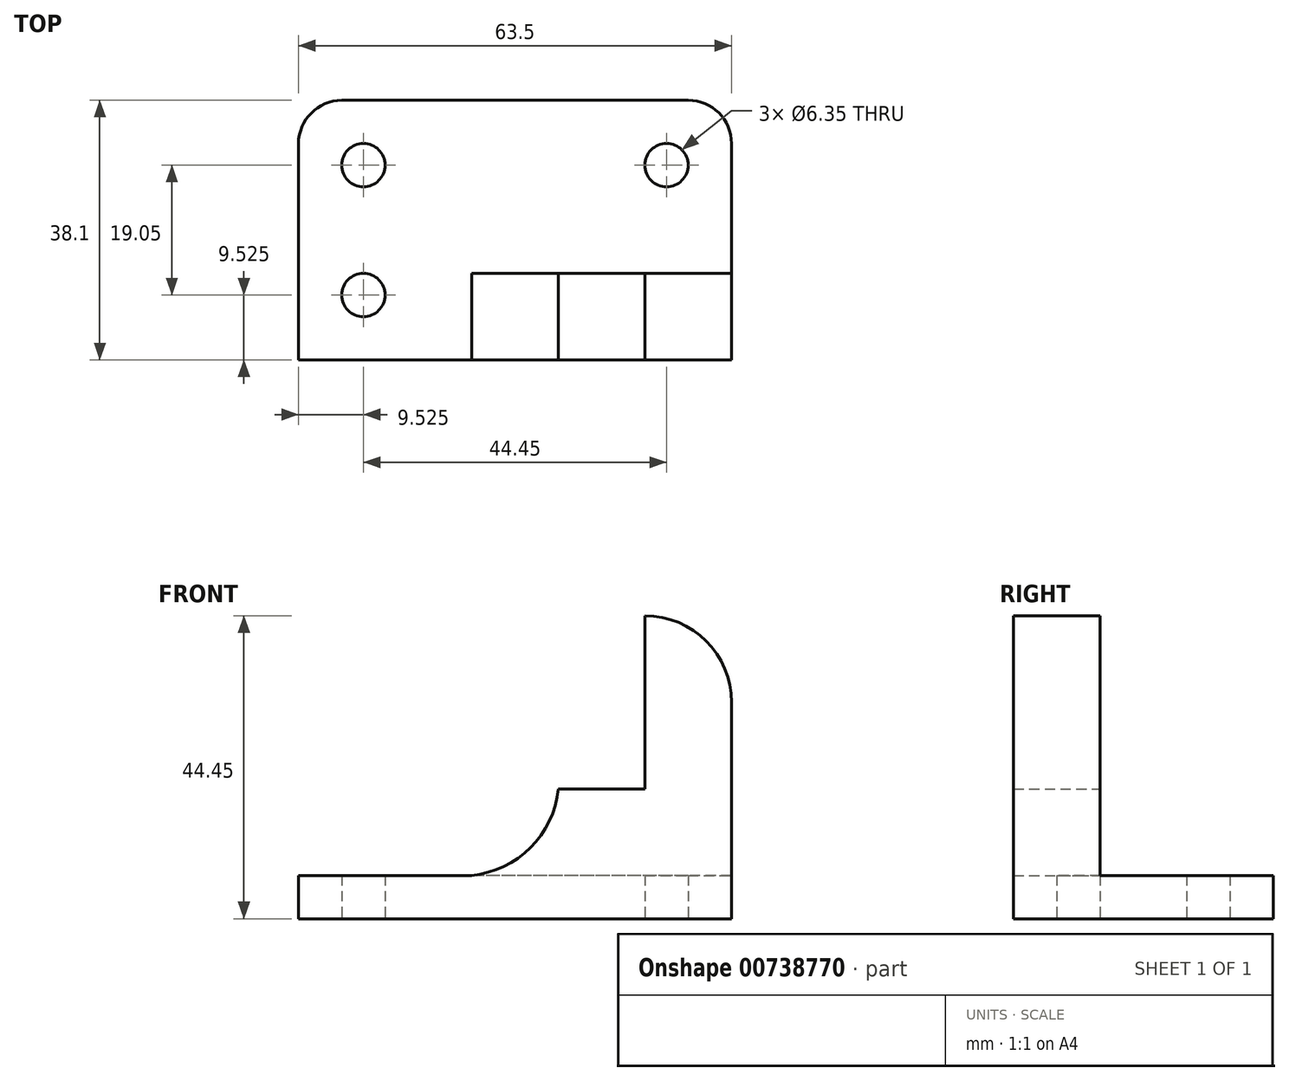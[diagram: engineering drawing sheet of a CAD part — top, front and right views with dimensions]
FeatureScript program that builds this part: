
annotation { "Feature Type Name" : "Feature", "Feature Type Description" : "" }
export const myFeature = defineFeature(function(context is Context, id is Id, definition is map)
    precondition{}
    {
        {
            var Q0;
            Q0=qCreatedBy(makeId("Front.planeOp"),FACE);
            var sketch = newSketch(context, id + "F0", { "sketchPlane" : qUnion([Q0])});
            skLineSegment(sketch, "E0", {"start": v(0, 0) * mm, "end": v(0, 44.45) * mm});
            skLineSegment(sketch, "E1", {"start": v(0, 44.45) * mm, "end": v(63.5, 44.45) * mm});
            skLineSegment(sketch, "E2", {"start": v(63.5, 44.45) * mm, "end": v(63.5, 0) * mm});
            skLineSegment(sketch, "E3", {"start": v(63.5, 0) * mm, "end": v(0, 0) * mm});
            skSolve(sketch);
        }
        {
            var Q0;
            Q0 = qSketchRegion(id + "F0", true);
            extrude(context, id + "F1", {"entities" : qUnion([Q0]), "depth" : 38.1 * mm, "offsetDistance" : 25.4 * mm});
        }
        {
            var Q0;
            Q0=qCreatedBy(makeId("Front.planeOp"),FACE);
            var sketch = newSketch(context, id + "F2", { "sketchPlane" : qUnion([Q0])});
            skLineSegment(sketch, "E4", {"start": v(0, 6.35) * mm, "end": v(0, 44.45) * mm});
            skLineSegment(sketch, "E5", {"start": v(0, 44.45) * mm, "end": v(63.5, 44.45) * mm});
            skLineSegment(sketch, "E6", {"start": v(63.5, 44.45) * mm, "end": v(63.5, 6.35) * mm});
            skLineSegment(sketch, "E7", {"start": v(63.5, 6.35) * mm, "end": v(0, 6.35) * mm});
            skSolve(sketch);
        }
        {
            var Q0;
            Q0 = qSketchRegion(id + "F2", true);
            extrude(context, id + "F3", {"entities" : qUnion([Q0]), "operationType" : NewBodyOperationType.REMOVE, "depth" : 25.4 * mm, "offsetDistance" : 25.4 * mm});
        }
        {
            var Q0;
            Q0=qCreatedBy(makeId("Front.planeOp"),FACE);
            var sketch = newSketch(context, id + "F4", { "sketchPlane" : qUnion([Q0])});
            skLineSegment(sketch, "E8", {"start": v(63.5, 31.75) * mm, "end": v(0, 31.75) * mm});
            skLineSegment(sketch, "E9", {"start": v(50.8, 44.45) * mm, "end": v(50.8, 6.35) * mm});
            skCircle(sketch, "E10", {"center": v(50.8, 31.75) * mm, "radius": 6.35 * mm});
            skLineSegment(sketch, "E11", {"start": v(38.1, 44.45) * mm, "end": v(38.1, 6.35) * mm});
            skArc(sketch, "E12", {"start": v(63.5, 31.75) * mm, "mid": v(50.8, 44.45) * mm, "end": v(38.1, 31.75) * mm});
            skLineSegment(sketch, "E13", {"start": v(63.5, 31.75) * mm, "end": v(63.5, 46.02) * mm});
            skLineSegment(sketch, "E14", {"start": v(63.5, 46.02) * mm, "end": v(38.12, 46.02) * mm});
            skLineSegment(sketch, "E15", {"start": v(38.12, 46.02) * mm, "end": v(38.1, 31.75) * mm});
            skLineSegment(sketch, "E16", {"start": v(63.5, 19.05) * mm, "end": v(0, 19.05) * mm});
            skLineSegment(sketch, "E17", {"start": v(25.4, 44.45) * mm, "end": v(25.4, 6.35) * mm});
            skArc(sketch, "E18", {"start": v(25.4, 6.35) * mm, "mid": v(34.03, 10.42) * mm, "end": v(38.1, 19.05) * mm});
            skSolve(sketch);
        }
        {
            var Q0;
            {var subQ0=sQuery(id+"F4.wireOp",EDGE,"E18");Q0=makeQuery(id+"F4.imprint","IMPRINT",FACE,{"disambiguationData":[TD([[makeQuery(id+"F4.imprint","IMPRINT",EDGE,{"derivedFrom":subQ0}),1.0]])]});}
            var Q1;
            {var subQ0=sQuery(id+"F4.wireOp",EDGE,"E10");var subQ1=sQuery(id+"F4.wireOp",EDGE,"E8");var subQ2=makeQuery(id+"F4.imprint","INTERSECT",VERTEX,{"disambiguationData":[OD(0.0)],"derivedFrom":[subQ1,subQ0]});Q1=makeQuery(id+"F4.imprint","IMPRINT",FACE,{"disambiguationData":[TD([[makeQuery(id+"F4.imprint","IMPRINT",EDGE,{"disambiguationData":[TD([[subQ2,-1.0]])],"derivedFrom":subQ1}),1.0]])]});}
            var Q2;
            {var subQ1=sQuery(id+"F4.wireOp",EDGE,"E8");var subQ3=sQuery(id+"F4.wireOp",EDGE,"E17");var subQ4=makeQuery(id+"F4.imprint","INTERSECT",VERTEX,{"derivedFrom":[subQ1,subQ3]});Q2=makeQuery(id+"F4.imprint","IMPRINT",FACE,{"disambiguationData":[TD([[makeQuery(id+"F4.imprint","IMPRINT",EDGE,{"disambiguationData":[TD([[subQ4,-1.0]])],"derivedFrom":subQ3}),1.0]])]});}
            var Q3;
            {var subQ1=sQuery(id+"F4.wireOp",EDGE,"E13");Q3=makeQuery(id+"F4.imprint","IMPRINT",FACE,{"disambiguationData":[TD([[makeQuery(id+"F4.imprint","IMPRINT",EDGE,{"derivedFrom":subQ1}),1.0]])]});}
            var Q4;
            {var subQ0=sQuery(id+"F4.wireOp",EDGE,"E10");var subQ1=sQuery(id+"F4.wireOp",EDGE,"E8");var subQ2=makeQuery(id+"F4.imprint","INTERSECT",VERTEX,{"disambiguationData":[OD(0.0)],"derivedFrom":[subQ1,subQ0]});Q4=makeQuery(id+"F4.imprint","IMPRINT",FACE,{"disambiguationData":[TD([[makeQuery(id+"F4.imprint","IMPRINT",EDGE,{"disambiguationData":[TD([[subQ2,-1.0]])],"derivedFrom":subQ1}),-1.0]])]});}
            var Q5;
            {var subQ0=sQuery(id+"F4.wireOp",EDGE,"E9");var subQ1=sQuery(id+"F4.wireOp",EDGE,"E8");var subQ2=makeQuery(id+"F4.imprint","INTERSECT",VERTEX,{"derivedFrom":[subQ1,subQ0]});Q5=makeQuery(id+"F4.imprint","IMPRINT",FACE,{"disambiguationData":[TD([[makeQuery(id+"F4.imprint","IMPRINT",EDGE,{"disambiguationData":[TD([[subQ2,-1.0]])],"derivedFrom":subQ1}),1.0]])]});}
            var Q6;
            {var subQ0=sQuery(id+"F4.wireOp",EDGE,"E9");var subQ1=sQuery(id+"F4.wireOp",EDGE,"E8");var subQ2=makeQuery(id+"F4.imprint","INTERSECT",VERTEX,{"derivedFrom":[subQ1,subQ0]});Q6=makeQuery(id+"F4.imprint","IMPRINT",FACE,{"disambiguationData":[TD([[makeQuery(id+"F4.imprint","IMPRINT",EDGE,{"disambiguationData":[TD([[subQ2,-1.0]])],"derivedFrom":subQ1}),-1.0]])]});}
            extrude(context, id + "F5", {"entities" : qUnion([Q0, Q1, Q2, Q3, Q4, Q5, Q6]), "operationType" : NewBodyOperationType.REMOVE, "endBound" : BoundingType.THROUGH_ALL, "depth" : 25.4 * mm, "offsetDistance" : 25.4 * mm});
        }
        {
            var Q0;
            Q0=qCreatedBy(makeId("Front.planeOp"),FACE);
            var sketch = newSketch(context, id + "F6", { "sketchPlane" : qUnion([Q0])});
            skLineSegment(sketch, "E19", {"start": v(38.1, 44.45) * mm, "end": v(38.1, 31.75) * mm});
            skLineSegment(sketch, "E20", {"start": v(38.1, 31.75) * mm, "end": v(25.4, 31.75) * mm});
            skLineSegment(sketch, "E21", {"start": v(25.4, 31.75) * mm, "end": v(25.4, 6.35) * mm});
            skLineSegment(sketch, "E22", {"start": v(25.4, 6.35) * mm, "end": v(0, 6.35) * mm});
            skLineSegment(sketch, "E23", {"start": v(0, 6.35) * mm, "end": v(0, 44.45) * mm});
            skLineSegment(sketch, "E24", {"start": v(0, 44.45) * mm, "end": v(38.1, 44.45) * mm});
            skLineSegment(sketch, "E25", {"start": v(38.1, 44.45) * mm, "end": v(38.13, 44.45) * mm});
            skLineSegment(sketch, "E26", {"start": v(38.13, 44.45) * mm, "end": v(38.1, 31.75) * mm});
            skSolve(sketch);
        }
        {
            var Q0;
            Q0 = qSketchRegion(id + "F6", true);
            extrude(context, id + "F7", {"entities" : qUnion([Q0]), "operationType" : NewBodyOperationType.REMOVE, "endBound" : BoundingType.THROUGH_ALL, "depth" : 25.4 * mm, "offsetDistance" : 25.4 * mm});
        }
        {
            var Q0;
            Q0=qCreatedBy(makeId("Top.planeOp"),FACE);
            var sketch = newSketch(context, id + "F8", { "sketchPlane" : qUnion([Q0])});
            skLineSegment(sketch, "E27", {"start": v(0, -6.35) * mm, "end": v(63.5, -6.35) * mm});
            skLineSegment(sketch, "E28", {"start": v(6.35, 0) * mm, "end": v(6.35, -38.1) * mm});
            skArc(sketch, "E29", {"start": v(6.35, 0) * mm, "mid": v(1.89, -1.89) * mm, "end": v(0, -6.35) * mm});
            skLineSegment(sketch, "E30", {"start": v(0, -6.35) * mm, "end": v(0, 0) * mm});
            skLineSegment(sketch, "E31", {"start": v(0, 0) * mm, "end": v(6.35, 0) * mm});
            skLineSegment(sketch, "E32", {"start": v(57.15, 0) * mm, "end": v(57.15, -25.4) * mm});
            skArc(sketch, "E33", {"start": v(63.5, -6.35) * mm, "mid": v(61.64, -1.86) * mm, "end": v(57.15, 0) * mm});
            skLineSegment(sketch, "E34", {"start": v(57.15, 0) * mm, "end": v(63.5, 0) * mm});
            skLineSegment(sketch, "E35", {"start": v(63.5, 0) * mm, "end": v(63.5, -6.35) * mm});
            skSolve(sketch);
        }
        {
            var Q0;
            Q0=makeQuery(id+"F8.imprint","IMPRINT",FACE,{"disambiguationData":[TD([[makeQuery(id+"F8.imprint","IMPRINT",EDGE,{"derivedFrom":sQuery(id+"F8.wireOp",EDGE,"E29")}),-1.0]])]});
            var Q1;
            Q1=makeQuery(id+"F8.imprint","IMPRINT",FACE,{"disambiguationData":[TD([[makeQuery(id+"F8.imprint","IMPRINT",EDGE,{"derivedFrom":sQuery(id+"F8.wireOp",EDGE,"E33")}),-1.0]])]});
            extrude(context, id + "F9", {"entities" : qUnion([Q0, Q1]), "operationType" : NewBodyOperationType.REMOVE, "depth" : 25.4 * mm, "offsetDistance" : 25.4 * mm});
        }
        {
            var Q0;
            Q0=qCreatedBy(makeId("Top.planeOp"),FACE);
            var sketch = newSketch(context, id + "F10", { "sketchPlane" : qUnion([Q0])});
            skLineSegment(sketch, "E36", {"start": v(0, -9.52) * mm, "end": v(63.5, -9.52) * mm});
            skLineSegment(sketch, "E37", {"start": v(9.52, 0) * mm, "end": v(9.53, -38.1) * mm});
            skLineSegment(sketch, "E38", {"start": v(53.97, 0) * mm, "end": v(53.97, -25.4) * mm});
            skCircle(sketch, "E39", {"center": v(9.52, -9.52) * mm, "radius": 3.18 * mm});
            skCircle(sketch, "E40", {"center": v(53.97, -9.52) * mm, "radius": 3.18 * mm});
            skLineSegment(sketch, "E41", {"start": v(-0.16, -28.58) * mm, "end": v(25.24, -28.57) * mm});
            skCircle(sketch, "E42", {"center": v(9.53, -28.58) * mm, "radius": 3.18 * mm});
            skSolve(sketch);
        }
        {
            var Q0;
            Q0 = qSketchRegion(id + "F10", true);
            extrude(context, id + "F11", {"entities" : qUnion([Q0]), "operationType" : NewBodyOperationType.REMOVE, "depth" : 25.4 * mm, "offsetDistance" : 25.4 * mm});
        }
    });
